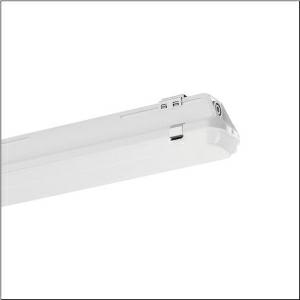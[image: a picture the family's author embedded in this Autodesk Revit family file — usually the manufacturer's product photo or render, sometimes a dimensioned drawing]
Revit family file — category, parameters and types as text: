
# Revit family: monsun_r__12_emergency_51fp107p437h3g_0806
name_source: partatom
category: Lighting Fixtures
units: mm (PartAtom-declared; Revit-internal decimal feet)

## family parameters
Cut with Voids When Loaded = No
Host = Face
Light Source = No
Part Type = Normal
Room Calculation Point = No
Round Connector Dimension = Use Diameter
Shared = No

## types (1)
- Monsun® 12 emergency (1 x LED, 3840 lm, 24.5 W, 4000K)
    Apparent Load = 25 VA
    CIE Flux Codes = 47 77 93 94 100
    Color Rendering = 80
    Color Temperature = 4000K
    Default Elevation = 1800 mm
    Description = Monsun® 12 emergency, damp-proof luminaire, chain hanger, primary optical cover: enclosure, of PMMA, light emission: direct distribution, primary light characteristic: symmetric, installation type: suspended mounting, surface-mounted, horizontal mounting, vertical mounting, LED rated luminous flux: 3.840 lm, light colour: 840, colour temperature: 4000K, control gear: ECG, with terminal, 4-pole, max. 2.5mm², mains connection: 220..240V, AC, 50/60Hz, rated input power: 25W, control gear: single battery element, battery: NiCd, 4,5 Ah, mains connection: 230V, 50Hz, luminaire housing, of glass-fibre reinforced polyester, uncoated, bright grey, length: 1.590 mm, width: 90 mm, height: 88mm, clip for enclosure, of stainless steel (V2A), ceiling mounting element, of stainless steel (V2A), chain hanger, of stainless steel (V2A), protection rating (complete): IP66, insulation class (complete): insulation class I (protective earthing), certification: CE, protection symbol: D, impact resistance: IK04, permissible ambient temperature for indoor applications: +5..+35°C, standard: EN 50419, EN 60598-2-1, EN 60598-2-22, no direct snow, no direct sun, no direct rain, for indoor or canopied outdoor use, corresponds to IFS (International Featured Standards) requirements for safety and quality in the food industry, packaging unit: 1 piece
    Height = 89 mm
    Lamp = 1 x LED
    Lamp Light Flux = 3840 lm
    Lamp Power = 24.5 W
    Lamp count = 1
    Length = 1590 mm
    Luminous efficacy = 157 lm/W
    Manufacturer = Siteco
    ModVariant = No
    Model = 51FP107P437H3G
    Mounting Place = Ceiling
    Mounting Type = Pendant
    Number of Poles = 1
    OnlyDefault = Yes
    Power Factor = 1
    Product Name = Monsun® 12 emergency
    Product group = damp-proof luminaire | ceiling pendant
    ProductGroupID = 908
    Protection Class = Protection class I
    Protection Degree = IP 66
    RLX_Detail_Level = 1
    RlxData = <blob elided: 88817 chars, md5=2119d7c4>
    Socket = socket
    Standby Power = 0 W
    System Light Flux = 3840 lm
    System Power = 25 W
    Type Comments = Product without accessories
    Type Image = l_1004748.jpg
    URL = http://relux.com
    VarID = ---
    Voltage = 0 V
    Weight = 0.00 kg
    Width = 90 mm

## geometry (parser evidence)
native form markers: Blend x4, Sweep x14
no freeform markers — native parametric forms only
